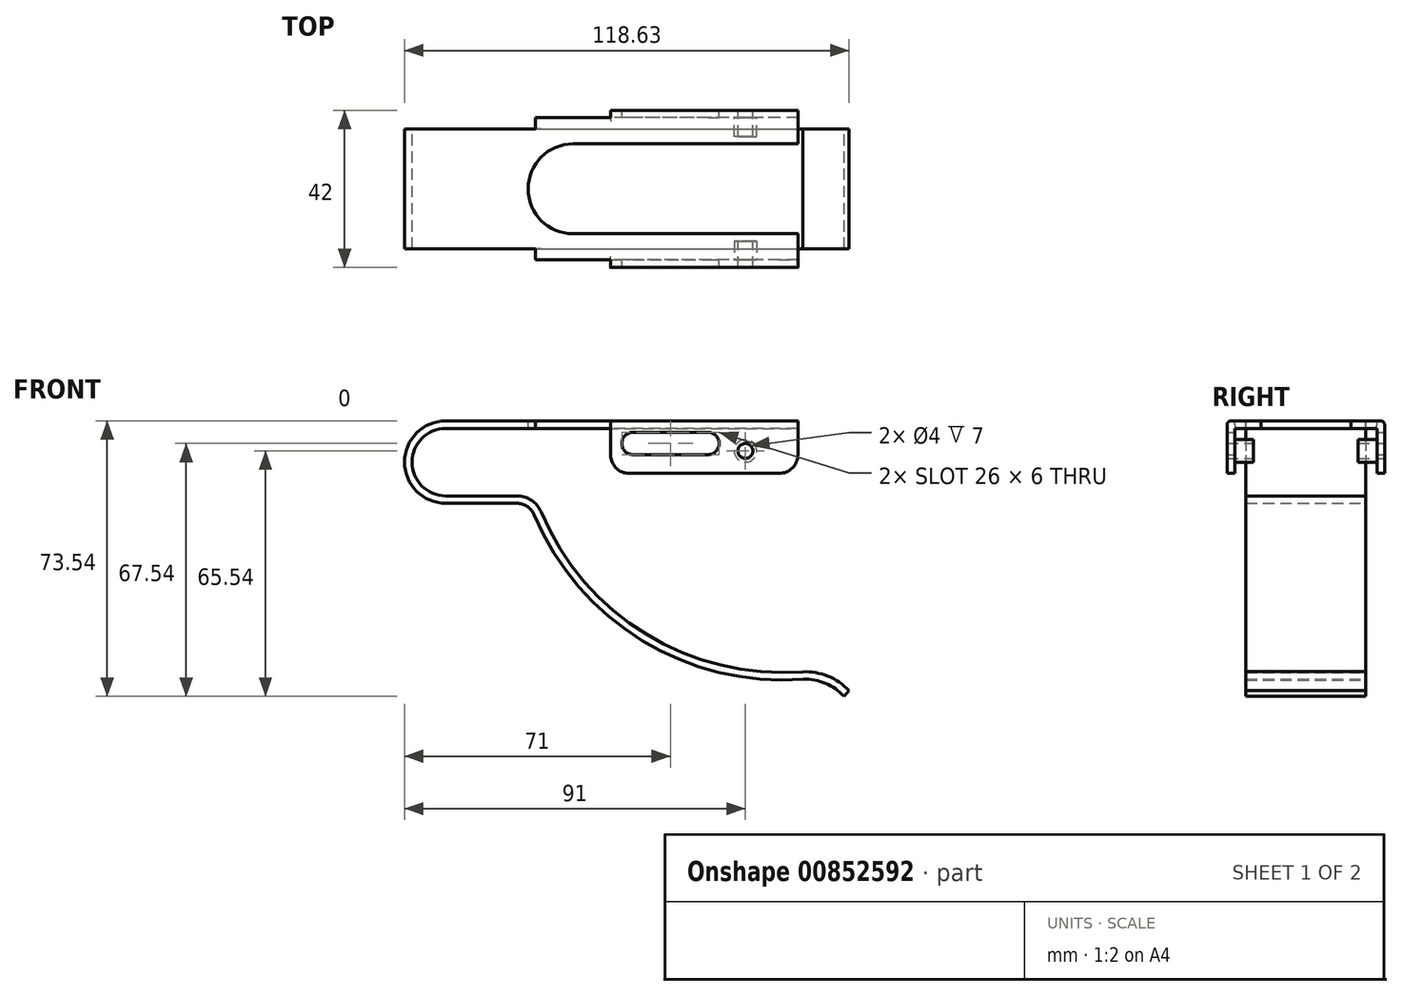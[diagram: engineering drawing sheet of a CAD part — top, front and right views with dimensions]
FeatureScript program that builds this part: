
annotation { "Feature Type Name" : "Feature", "Feature Type Description" : "" }
export const myFeature = defineFeature(function(context is Context, id is Id, definition is map)
    precondition{}
    {
        {
            var Q0;
            Q0=qCreatedBy(makeId("Front.planeOp"),FACE);
            var sketch = newSketch(context, id + "F0", { "sketchPlane" : qUnion([Q0])});
            skArc(sketch, "E0", {"start": v(0, 11) * mm, "mid": v(-11, 0) * mm, "end": v(0, -11) * mm});
            skLineSegment(sketch, "E1", {"start": v(0, 11) * mm, "end": v(94, 11) * mm});
            skLineSegment(sketch, "E2", {"start": v(0, -11) * mm, "end": v(19, -11) * mm});
            skArc(sketch, "E3", {"start": v(23.61, -14.06) * mm, "mid": v(52.42, -47.62) * mm, "end": v(95.41, -58) * mm});
            skArc(sketch, "E4", {"start": v(106.34, -62.54) * mm, "mid": v(101.38, -59.06) * mm, "end": v(95.41, -58) * mm});
            skPoint(sketch, "E5.visualSharp", {"position": v(22.4, -11) * mm});
            skArc(sketch, "E5.filletArc", {"start": v(23.61, -14.06) * mm, "mid": v(21.77, -11.84) * mm, "end": v(19, -11) * mm});
            skArc(sketch, "E6.0", {"start": v(107.63, -61) * mm, "mid": v(102, -57.16) * mm, "end": v(95.3, -56) * mm});
            skArc(sketch, "E6.1", {"start": v(25.45, -13.3) * mm, "mid": v(53.48, -45.92) * mm, "end": v(95.3, -56) * mm});
            skLineSegment(sketch, "E6.2", {"start": v(0, 9) * mm, "end": v(94, 9) * mm});
            skArc(sketch, "E6.3", {"start": v(0, 9) * mm, "mid": v(-9, 0) * mm, "end": v(0, -9) * mm});
            skLineSegment(sketch, "E6.4", {"start": v(0, -9) * mm, "end": v(19, -9) * mm});
            skArc(sketch, "E6.5", {"start": v(25.45, -13.3) * mm, "mid": v(22.88, -10.17) * mm, "end": v(19, -9) * mm});
            skLineSegment(sketch, "E7", {"start": v(94, 11) * mm, "end": v(94, 9) * mm});
            skLineSegment(sketch, "E8", {"start": v(106.34, -62.54) * mm, "end": v(107.63, -61) * mm});
            skSolve(sketch);
        }
        {
            var Q0;
            Q0 = qSketchRegion(id + "F0", true);
            extrude(context, id + "F1", {"entities" : qUnion([Q0]), "depth" : 16 * mm, "offsetDistance" : 25 * mm});
        }
        {
            var Q0;
            Q0=makeQuery(id+"F1.opExtrude","SWEPT_FACE",FACE,{"disambiguationData":[OSD([sQuery(id+"F0.wireOp",EDGE,"E1")])]});
            var sketch = newSketch(context, id + "F2", { "sketchPlane" : qUnion([Q0])});
            skLineSegment(sketch, "E9.bottom", {"start": v(94, -16) * mm, "end": v(24, -16) * mm});
            skLineSegment(sketch, "E9.top", {"start": v(94, -19) * mm, "end": v(24, -19) * mm});
            skLineSegment(sketch, "E9.left", {"start": v(94, -16) * mm, "end": v(94, -19) * mm});
            skLineSegment(sketch, "E9.right", {"start": v(24, -16) * mm, "end": v(24, -19) * mm});
            skSolve(sketch);
        }
        {
            var Q0;
            Q0=makeQuery(id+"F2.imprint","IMPRINT",FACE,{"disambiguationData":[TD([[makeQuery(id+"F2.imprint","IMPRINT",EDGE,{"derivedFrom":sQuery(id+"F2.wireOp",EDGE,"E9.bottom")}),-1.0]])]});
            extrude(context, id + "F3", {"entities" : qUnion([Q0]), "operationType" : NewBodyOperationType.ADD, "oppositeDirection" : true, "depth" : 2 * mm, "offsetDistance" : 25 * mm});
        }
        {
            var Q0;
            Q0=makeQuery(id+"F3.opExtrude","SWEPT_FACE",FACE,{"disambiguationData":[OSD([sQuery(id+"F2.wireOp",EDGE,"E9.top")])]});
            var sketch = newSketch(context, id + "F4", { "sketchPlane" : qUnion([Q0])});
            skLineSegment(sketch, "E10.bottom", {"start": v(94, 11) * mm, "end": v(44, 11) * mm});
            skLineSegment(sketch, "E10.top", {"start": v(94, -3) * mm, "end": v(44, -3) * mm});
            skLineSegment(sketch, "E10.left", {"start": v(94, 11) * mm, "end": v(94, -3) * mm});
            skLineSegment(sketch, "E10.right", {"start": v(44, 11) * mm, "end": v(44, -3) * mm});
            skSolve(sketch);
        }
        {
            var Q0;
            Q0 = qSketchRegion(id + "F4", true);
            extrude(context, id + "F5", {"entities" : qUnion([Q0]), "operationType" : NewBodyOperationType.ADD, "depth" : 2 * mm, "offsetDistance" : 25 * mm});
        }
        {
            var Q0;
            Q0=makeQuery(id+"F5.opExtrude","CAP_EDGE",EDGE,{"disambiguationData":[OSD([sQuery(id+"F4.wireOp",EDGE,"E10.bottom")])],"isStart":false});
            var Q1;
            {var subQ0=sQuery(id+"F2.wireOp",EDGE,"E9.top");Q1=makeQuery(id+"F5.boolean.opBoolean","SPLIT",EDGE,{"disambiguationData":[topologyDisambiguationEdgeConnected([makeQuery(id+"F5.opExtrude","CAP_FACE",FACE,{"disambiguationData":[OSD([sQuery(id+"F4.wireOp",EDGE,"E10.bottom"),sQuery(id+"F4.wireOp",EDGE,"E10.top"),sQuery(id+"F4.wireOp",EDGE,"E10.left"),sQuery(id+"F4.wireOp",EDGE,"E10.right")])],"isStart":true})])],"derivedFrom":makeQuery(id+"F3.opExtrude","CAP_EDGE",EDGE,{"disambiguationData":[OSD([subQ0])],"isStart":false})});}
            fillet(context, id + "F6", {"entities" : qUnion([Q0, Q1]), "radius" : 1 * mm, "tangentPropagation" : true, "allowEdgeOverflow" : false});
        }
        {
            var Q0;
            Q0=makeQuery(id+"F1.opExtrude","SWEPT_BODY",BODY,{"disambiguationData":[OSD([sQuery(id+"F0.wireOp",EDGE,"E0"),sQuery(id+"F0.wireOp",EDGE,"E1"),sQuery(id+"F0.wireOp",EDGE,"E2"),sQuery(id+"F0.wireOp",EDGE,"E3"),sQuery(id+"F0.wireOp",EDGE,"E4"),sQuery(id+"F0.wireOp",EDGE,"E5.filletArc"),sQuery(id+"F0.wireOp",EDGE,"E6.0"),sQuery(id+"F0.wireOp",EDGE,"E6.1"),sQuery(id+"F0.wireOp",EDGE,"E6.2"),sQuery(id+"F0.wireOp",EDGE,"E6.3"),sQuery(id+"F0.wireOp",EDGE,"E6.4"),sQuery(id+"F0.wireOp",EDGE,"E6.5"),sQuery(id+"F0.wireOp",EDGE,"E7"),sQuery(id+"F0.wireOp",EDGE,"E8")])]});
            var Q1;
            Q1=qCreatedBy(makeId("Front.planeOp"),FACE);
            mirror(context, id + "F7", {"operationType" : NewBodyOperationType.ADD, "entities" : qUnion([Q0]), "mirrorPlane" : qUnion([Q1])});
        }
        {
            var Q0;
            {var subQ0=makeQuery(id+"F5.boolean.opBoolean","MERGE",FACE,{"derivedFrom":[makeQuery(id+"F3.boolean.opBoolean","MERGE",FACE,{"derivedFrom":[makeQuery(id+"F1.opExtrude","SWEPT_FACE",FACE,{"disambiguationData":[OSD([sQuery(id+"F0.wireOp",EDGE,"E1")])]}),makeQuery(id+"F3.opExtrude","CAP_FACE",FACE,{"disambiguationData":[OSD([sQuery(id+"F2.wireOp",EDGE,"E9.bottom"),sQuery(id+"F2.wireOp",EDGE,"E9.top"),sQuery(id+"F2.wireOp",EDGE,"E9.left"),sQuery(id+"F2.wireOp",EDGE,"E9.right")])],"isStart":true})]}),makeQuery(id+"F5.opExtrude","SWEPT_FACE",FACE,{"disambiguationData":[OSD([sQuery(id+"F4.wireOp",EDGE,"E10.bottom")])]})]});Q0=makeQuery(id+"F7.boolean.opBoolean","MERGE",FACE,{"derivedFrom":[subQ0,makeQuery(id+"F7.opPattern","COPY",FACE,{"derivedFrom":subQ0,"instanceName":"1"})]});}
            var sketch = newSketch(context, id + "F8", { "sketchPlane" : qUnion([Q0])});
            skArc(sketch, "E11", {"start": v(34, 12) * mm, "mid": v(22, 0) * mm, "end": v(34, -12) * mm});
            skLineSegment(sketch, "E12", {"start": v(34, 12) * mm, "end": v(94, 12) * mm});
            skLineSegment(sketch, "E13", {"start": v(94, 12) * mm, "end": v(94, -12) * mm});
            skLineSegment(sketch, "E14", {"start": v(94, -12) * mm, "end": v(34, -12) * mm});
            skSolve(sketch);
        }
        {
            var Q0;
            Q0 = qSketchRegion(id + "F8", true);
            extrude(context, id + "F9", {"entities" : qUnion([Q0]), "operationType" : NewBodyOperationType.REMOVE, "oppositeDirection" : true, "depth" : 2 * mm, "offsetDistance" : 25 * mm});
        }
        {
            var Q0;
            Q0=makeQuery(id+"F7.opPattern","COPY",FACE,{"derivedFrom":makeQuery(id+"F5.opExtrude","CAP_FACE",FACE,{"disambiguationData":[OSD([sQuery(id+"F4.wireOp",EDGE,"E10.bottom"),sQuery(id+"F4.wireOp",EDGE,"E10.top"),sQuery(id+"F4.wireOp",EDGE,"E10.left"),sQuery(id+"F4.wireOp",EDGE,"E10.right")])],"isStart":false}),"instanceName":"1"});
            var sketch = newSketch(context, id + "F10", { "sketchPlane" : qUnion([Q0])});
            skLineSegment(sketch, "E15", {"start": v(-70, 5) * mm, "end": v(-50, 5) * mm});
            skArc(sketch, "E16.0.startCap", {"start": v(-70, 2) * mm, "mid": v(-73, 5) * mm, "end": v(-70, 8) * mm});
            skArc(sketch, "E16.0.endCap", {"start": v(-50, 8) * mm, "mid": v(-47, 5) * mm, "end": v(-50, 2) * mm});
            skLineSegment(sketch, "E16.0.left", {"start": v(-70, 8) * mm, "end": v(-50, 8) * mm});
            skLineSegment(sketch, "E16.0.right", {"start": v(-70, 2) * mm, "end": v(-50, 2) * mm});
            skSolve(sketch);
        }
        {
            var Q0;
            Q0 = qSketchRegion(id + "F10", true);
            extrude(context, id + "F11", {"entities" : qUnion([Q0]), "operationType" : NewBodyOperationType.REMOVE, "endBound" : BoundingType.THROUGH_ALL, "oppositeDirection" : true, "depth" : 25 * mm, "offsetDistance" : 25 * mm});
        }
        {
            var Q0;
            Q0=makeQuery(id+"F7.opPattern","COPY",FACE,{"derivedFrom":makeQuery(id+"F5.opExtrude","CAP_FACE",FACE,{"disambiguationData":[OSD([sQuery(id+"F4.wireOp",EDGE,"E10.bottom"),sQuery(id+"F4.wireOp",EDGE,"E10.top"),sQuery(id+"F4.wireOp",EDGE,"E10.left"),sQuery(id+"F4.wireOp",EDGE,"E10.right")])],"isStart":false}),"instanceName":"1"});
            var sketch = newSketch(context, id + "F12", { "sketchPlane" : qUnion([Q0])});
            skPoint(sketch, "E17", {"position": v(-80, 3) * mm});
            skSolve(sketch);
        }
        {
            var Q0;
            Q0=sQuery(id+"F12.wireOp",VERTEX,"E17");
            var Q1;
            Q1=makeQuery(id+"F1.opExtrude","SWEPT_BODY",BODY,{"disambiguationData":[OSD([sQuery(id+"F0.wireOp",EDGE,"E0"),sQuery(id+"F0.wireOp",EDGE,"E1"),sQuery(id+"F0.wireOp",EDGE,"E2"),sQuery(id+"F0.wireOp",EDGE,"E3"),sQuery(id+"F0.wireOp",EDGE,"E4"),sQuery(id+"F0.wireOp",EDGE,"E5.filletArc"),sQuery(id+"F0.wireOp",EDGE,"E6.0"),sQuery(id+"F0.wireOp",EDGE,"E6.1"),sQuery(id+"F0.wireOp",EDGE,"E6.2"),sQuery(id+"F0.wireOp",EDGE,"E6.3"),sQuery(id+"F0.wireOp",EDGE,"E6.4"),sQuery(id+"F0.wireOp",EDGE,"E6.5"),sQuery(id+"F0.wireOp",EDGE,"E7"),sQuery(id+"F0.wireOp",EDGE,"E8")])]});
            hole(context, id + "F13", {"style" : HoleStyle.SIMPLE, "endStyle" : HoleEndStyle.THROUGH, "holeDiameter" : 4 * mm, "majorDiameter" : 5 * mm, "isTappedThrough" : true, "tappedDepth" : 12 * mm, "tapClearance" : 3, "locations" : qUnion([Q0]), "scope" : qUnion([Q1])});
        }
        {
            var Q0;
            Q0=makeQuery(id+"F7.opPattern","COPY",FACE,{"derivedFrom":makeQuery(id+"F5.opExtrude","CAP_FACE",FACE,{"disambiguationData":[OSD([sQuery(id+"F4.wireOp",EDGE,"E10.bottom"),sQuery(id+"F4.wireOp",EDGE,"E10.top"),sQuery(id+"F4.wireOp",EDGE,"E10.left"),sQuery(id+"F4.wireOp",EDGE,"E10.right")])],"isStart":true}),"instanceName":"1"});
            var sketch = newSketch(context, id + "F14", { "sketchPlane" : qUnion([Q0])});
            skCircle(sketch, "E18.0", {"center": v(80, 3) * mm, "radius": 2 * mm});
            skCircle(sketch, "E19.0", {"center": v(80, 3) * mm, "radius": 3 * mm});
            skSolve(sketch);
        }
        {
            var Q0;
            Q0=makeQuery(id+"F14.imprint","IMPRINT",FACE,{"disambiguationData":[TD([[makeQuery(id+"F14.imprint","IMPRINT",EDGE,{"derivedFrom":sQuery(id+"F14.wireOp",EDGE,"E18.0")}),-1.0]])]});
            extrude(context, id + "F15", {"entities" : qUnion([Q0]), "operationType" : NewBodyOperationType.ADD, "depth" : 5 * mm, "offsetDistance" : 25 * mm});
        }
        {
            var Q0;
            Q0=makeQuery(id+"F1.opExtrude","SWEPT_BODY",BODY,{"disambiguationData":[OSD([sQuery(id+"F0.wireOp",EDGE,"E0"),sQuery(id+"F0.wireOp",EDGE,"E1"),sQuery(id+"F0.wireOp",EDGE,"E2"),sQuery(id+"F0.wireOp",EDGE,"E3"),sQuery(id+"F0.wireOp",EDGE,"E4"),sQuery(id+"F0.wireOp",EDGE,"E5.filletArc"),sQuery(id+"F0.wireOp",EDGE,"E6.0"),sQuery(id+"F0.wireOp",EDGE,"E6.1"),sQuery(id+"F0.wireOp",EDGE,"E6.2"),sQuery(id+"F0.wireOp",EDGE,"E6.3"),sQuery(id+"F0.wireOp",EDGE,"E6.4"),sQuery(id+"F0.wireOp",EDGE,"E6.5"),sQuery(id+"F0.wireOp",EDGE,"E7"),sQuery(id+"F0.wireOp",EDGE,"E8")])]});
            var Q1;
            Q1=qCreatedBy(makeId("Front.planeOp"),FACE);
            mirror(context, id + "F16", {"operationType" : NewBodyOperationType.ADD, "entities" : qUnion([Q0]), "mirrorPlane" : qUnion([Q1])});
        }
        {
            var Q0;
            Q0=makeQuery(id+"F7.opPattern","COPY",EDGE,{"derivedFrom":makeQuery(id+"F5.opExtrude","SWEPT_EDGE",EDGE,{"disambiguationData":[OSD([sQuery(id+"F4.wireOp",EDGE,"E10.top"),sQuery(id+"F4.wireOp",EDGE,"E10.left")])]}),"instanceName":"1"});
            var Q1;
            Q1=makeQuery(id+"F7.opPattern","COPY",EDGE,{"derivedFrom":makeQuery(id+"F5.opExtrude","SWEPT_EDGE",EDGE,{"disambiguationData":[OSD([sQuery(id+"F4.wireOp",EDGE,"E10.top"),sQuery(id+"F4.wireOp",EDGE,"E10.right")])]}),"instanceName":"1"});
            var Q2;
            Q2=makeQuery(id+"F5.opExtrude","SWEPT_EDGE",EDGE,{"disambiguationData":[OSD([sQuery(id+"F4.wireOp",EDGE,"E10.top"),sQuery(id+"F4.wireOp",EDGE,"E10.left")])]});
            var Q3;
            Q3=makeQuery(id+"F5.opExtrude","SWEPT_EDGE",EDGE,{"disambiguationData":[OSD([sQuery(id+"F4.wireOp",EDGE,"E10.top"),sQuery(id+"F4.wireOp",EDGE,"E10.right")])]});
            fillet(context, id + "F17", {"entities" : qUnion([Q0, Q1, Q2, Q3]), "radius" : 5 * mm, "tangentPropagation" : true, "allowEdgeOverflow" : false});
        }
    });
